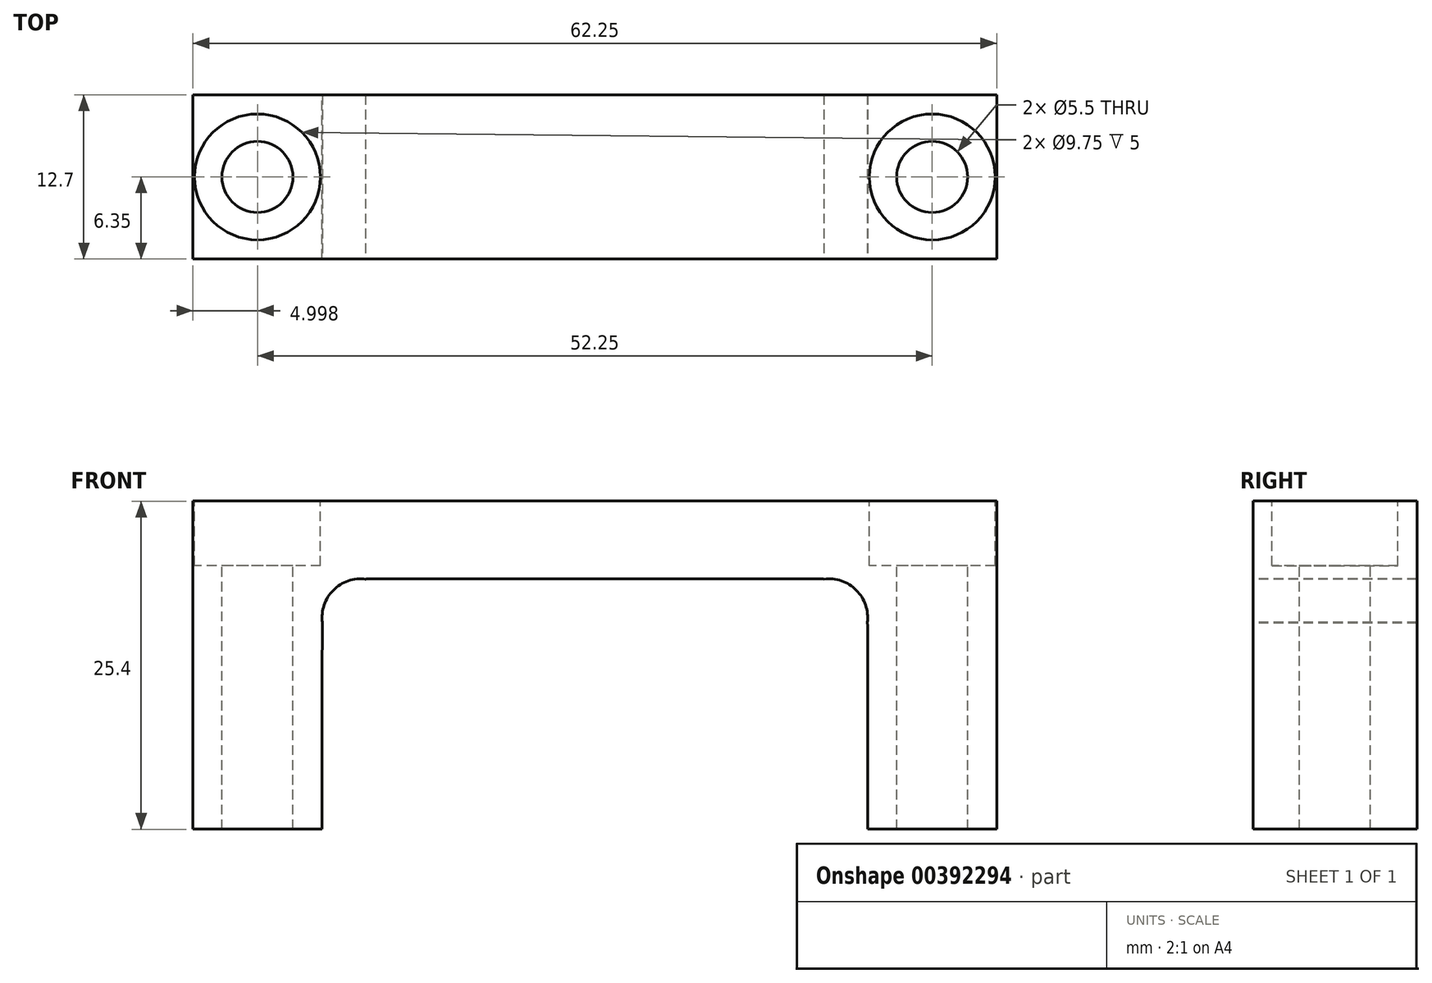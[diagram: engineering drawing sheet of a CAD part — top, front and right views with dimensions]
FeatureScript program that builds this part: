
annotation { "Feature Type Name" : "Feature", "Feature Type Description" : "" }
export const myFeature = defineFeature(function(context is Context, id is Id, definition is map)
    precondition{}
    {
        {
            var Q0;
            Q0=qCreatedBy(makeId("Front.planeOp"),FACE);
            var sketch = newSketch(context, id + "F0", { "sketchPlane" : qUnion([Q0])});
            skLineSegment(sketch, "E0", {"start": v(-31.41, -12.39) * mm, "end": v(-21.41, -12.39) * mm});
            skLineSegment(sketch, "E1", {"start": v(-21.41, -12.39) * mm, "end": v(-21.41, -0.6) * mm});
            skLineSegment(sketch, "E2", {"start": v(-21.41, -0.6) * mm, "end": v(-13.81, 7) * mm});
            skLineSegment(sketch, "E3", {"start": v(-13.81, 7) * mm, "end": v(13.24, 7) * mm});
            skLineSegment(sketch, "E4", {"start": v(13.24, 7) * mm, "end": v(20.84, -0.6) * mm});
            skLineSegment(sketch, "E5", {"start": v(20.84, -0.6) * mm, "end": v(20.84, -12.39) * mm});
            skLineSegment(sketch, "E6", {"start": v(20.84, -12.39) * mm, "end": v(30.84, -12.39) * mm});
            skLineSegment(sketch, "E7", {"start": v(-26.41, 13.01) * mm, "end": v(25.84, 13.01) * mm});
            skLineSegment(sketch, "E8", {"start": v(-31.41, 5.41) * mm, "end": v(-31.41, -12.39) * mm});
            skLineSegment(sketch, "E9", {"start": v(30.84, 5.41) * mm, "end": v(30.84, -12.39) * mm});
            skLineSegment(sketch, "E10", {"start": v(-26.41, 13.01) * mm, "end": v(-31.41, 13.01) * mm});
            skLineSegment(sketch, "E11", {"start": v(-31.41, 13.01) * mm, "end": v(-31.41, 2.42) * mm});
            skLineSegment(sketch, "E12", {"start": v(25.84, 13.01) * mm, "end": v(30.84, 13.01) * mm});
            skLineSegment(sketch, "E13", {"start": v(30.84, 13.01) * mm, "end": v(30.84, 5.41) * mm});
            skSolve(sketch);
        }
        {
            var Q0;
            Q0 = qSketchRegion(id + "F0", true);
            extrude(context, id + "F1", {"entities" : qUnion([Q0]), "endBound" : BoundingType.SYMMETRIC, "depth" : 12.7 * mm});
        }
        {
            var Q0;
            Q0=makeQuery(id+"F1.opExtrude","SWEPT_FACE",FACE,{"disambiguationData":[OSD([sQuery(id+"F0.wireOp",EDGE,"E7"),sQuery(id+"F0.wireOp",EDGE,"E10"),sQuery(id+"F0.wireOp",EDGE,"E12")])]});
            var sketch = newSketch(context, id + "F2", { "sketchPlane" : qUnion([Q0])});
            skPoint(sketch, "E14", {"position": v(-26.41, 0) * mm});
            skPoint(sketch, "E15", {"position": v(25.84, 0) * mm});
            skSolve(sketch);
        }
        {
            var Q0;
            Q0=sQuery(id+"F2.wireOp",VERTEX,"E15");
            var Q1;
            Q1=sQuery(id+"F2.wireOp",VERTEX,"E14");
            var Q2;
            Q2=makeQuery(id+"F1.opExtrude","SWEPT_BODY",BODY,{"disambiguationData":[OSD([sQuery(id+"F0.wireOp",EDGE,"E0"),sQuery(id+"F0.wireOp",EDGE,"E1"),sQuery(id+"F0.wireOp",EDGE,"E2"),sQuery(id+"F0.wireOp",EDGE,"E3"),sQuery(id+"F0.wireOp",EDGE,"E4"),sQuery(id+"F0.wireOp",EDGE,"E5"),sQuery(id+"F0.wireOp",EDGE,"E6"),sQuery(id+"F0.wireOp",EDGE,"E7"),sQuery(id+"F0.wireOp",EDGE,"E8"),sQuery(id+"F0.wireOp",EDGE,"E9"),sQuery(id+"F0.wireOp",EDGE,"E10"),sQuery(id+"F0.wireOp",EDGE,"E11"),sQuery(id+"F0.wireOp",EDGE,"E12"),sQuery(id+"F0.wireOp",EDGE,"E13")])]});
            hole(context, id + "F3", {"style" : HoleStyle.C_BORE, "endStyle" : HoleEndStyle.THROUGH, "standardTappedOrClearance" : lookupTablePath({ "standard" : "ISO", "fit" : "Normal", "size" : "M5", "type" : "Clearance" }), "standardBlindInLast" : lookupTablePath({ "fit" : "Standard", "standard" : "ISO", "size" : "M5", "type" : "Clearance" }), "holeDiameter" : 5.5 * mm, "cBoreDiameter" : 9.75 * mm, "cBoreDepth" : 5 * mm, "isTappedThrough" : true, "tappedDepth" : 12 * mm, "tapClearance" : 3, "startFromSketch" : true, "locations" : qUnion([Q0, Q1]), "scope" : qUnion([Q2])});
        }
        {
            var Q0;
            Q0=makeQuery(id+"F1.opExtrude","CAP_FACE",FACE,{"disambiguationData":[OSD([sQuery(id+"F0.wireOp",EDGE,"E0"),sQuery(id+"F0.wireOp",EDGE,"E1"),sQuery(id+"F0.wireOp",EDGE,"E2"),sQuery(id+"F0.wireOp",EDGE,"E3"),sQuery(id+"F0.wireOp",EDGE,"E4"),sQuery(id+"F0.wireOp",EDGE,"E5"),sQuery(id+"F0.wireOp",EDGE,"E6"),sQuery(id+"F0.wireOp",EDGE,"E7"),sQuery(id+"F0.wireOp",EDGE,"E8"),sQuery(id+"F0.wireOp",EDGE,"E9"),sQuery(id+"F0.wireOp",EDGE,"E10"),sQuery(id+"F0.wireOp",EDGE,"E11"),sQuery(id+"F0.wireOp",EDGE,"E12"),sQuery(id+"F0.wireOp",EDGE,"E13")])],"isStart":false});
            var sketch = newSketch(context, id + "F4", { "sketchPlane" : qUnion([Q0])});
            skCircle(sketch, "E16", {"center": v(-17.61, 3.2) * mm, "radius": 3.8 * mm});
            skLineSegment(sketch, "E17", {"start": v(-13.81, 7) * mm, "end": v(-17.61, 7) * mm});
            skLineSegment(sketch, "E18", {"start": v(-21.41, -0.6) * mm, "end": v(-21.4, 3.57) * mm});
            skCircle(sketch, "E19", {"center": v(17.04, 3.2) * mm, "radius": 3.8 * mm});
            skLineSegment(sketch, "E20", {"start": v(13.24, 7) * mm, "end": v(17.04, 7) * mm});
            skLineSegment(sketch, "E21", {"start": v(20.84, -0.6) * mm, "end": v(20.84, 3.2) * mm});
            skLineSegment(sketch, "E22", {"start": v(20.84, 3.2) * mm, "end": v(20.89, 3.45) * mm});
            skSolve(sketch);
        }
        {
            var Q0;
            {var subQ0=sQuery(id+"F4.wireOp",EDGE,"E17");Q0=makeQuery(id+"F4.imprint","IMPRINT",FACE,{"disambiguationData":[TD([[makeQuery(id+"F4.imprint","IMPRINT",EDGE,{"derivedFrom":subQ0}),1.0]])]});}
            var Q1;
            {var subQ0=sQuery(id+"F4.wireOp",EDGE,"E18");var subQ1=sQuery(id+"F4.wireOp",EDGE,"E16");var subQ2=makeQuery(id+"F4.imprint","INTERSECT",VERTEX,{"disambiguationData":[OD(1.0)],"derivedFrom":[subQ1,subQ0]});Q1=makeQuery(id+"F4.imprint","IMPRINT",FACE,{"disambiguationData":[TD([[makeQuery(id+"F4.imprint","IMPRINT",EDGE,{"disambiguationData":[TD([[subQ2,-1.0]])],"derivedFrom":subQ1}),-1.0]])]});}
            var Q2;
            {var subQ1=sQuery(id+"F4.wireOp",EDGE,"E16");var subQ6=makeQuery(id+"F4.imprint","INTERSECT",VERTEX,{"derivedFrom":[subQ1,sQuery(id+"F4.wireOp",EDGE,"E17")]});Q2=makeQuery(id+"F4.imprint","IMPRINT",FACE,{"disambiguationData":[TD([[makeQuery(id+"F4.imprint","IMPRINT",EDGE,{"disambiguationData":[TD([[subQ6,1.0]])],"derivedFrom":subQ1}),1.0]])]});}
            extrude(context, id + "F5", {"entities" : qUnion([Q0, Q1, Q2]), "operationType" : NewBodyOperationType.REMOVE, "endBound" : BoundingType.THROUGH_ALL, "oppositeDirection" : true, "depth" : 25 * mm});
        }
        {
            var Q0;
            Q0=makeQuery(id+"F1.opExtrude","CAP_FACE",FACE,{"disambiguationData":[OSD([sQuery(id+"F0.wireOp",EDGE,"E0"),sQuery(id+"F0.wireOp",EDGE,"E1"),sQuery(id+"F0.wireOp",EDGE,"E2"),sQuery(id+"F0.wireOp",EDGE,"E3"),sQuery(id+"F0.wireOp",EDGE,"E4"),sQuery(id+"F0.wireOp",EDGE,"E5"),sQuery(id+"F0.wireOp",EDGE,"E6"),sQuery(id+"F0.wireOp",EDGE,"E7"),sQuery(id+"F0.wireOp",EDGE,"E8"),sQuery(id+"F0.wireOp",EDGE,"E9"),sQuery(id+"F0.wireOp",EDGE,"E10"),sQuery(id+"F0.wireOp",EDGE,"E11"),sQuery(id+"F0.wireOp",EDGE,"E12"),sQuery(id+"F0.wireOp",EDGE,"E13")])],"isStart":false});
            var sketch = newSketch(context, id + "F6", { "sketchPlane" : qUnion([Q0])});
            skCircle(sketch, "E23", {"center": v(17.04, 3.2) * mm, "radius": 3.8 * mm});
            skLineSegment(sketch, "E24", {"start": v(13.24, 7) * mm, "end": v(17.04, 7) * mm});
            skLineSegment(sketch, "E25", {"start": v(20.84, -0.6) * mm, "end": v(20.84, 3.2) * mm});
            skSolve(sketch);
        }
        {
            var Q0;
            {var subQ0=sQuery(id+"F6.wireOp",EDGE,"E23");var subQ1=makeQuery(id+"F6.imprint","INTERSECT",VERTEX,{"derivedFrom":[subQ0,sQuery(id+"F6.wireOp",EDGE,"E24")]});Q0=makeQuery(id+"F6.imprint","IMPRINT",FACE,{"disambiguationData":[TD([[makeQuery(id+"F6.imprint","IMPRINT",EDGE,{"disambiguationData":[TD([[subQ1,1.0]])],"derivedFrom":subQ0}),1.0]])]});}
            var Q1;
            {var subQ0=sQuery(id+"F6.wireOp",EDGE,"E24");Q1=makeQuery(id+"F6.imprint","IMPRINT",FACE,{"disambiguationData":[TD([[makeQuery(id+"F6.imprint","IMPRINT",EDGE,{"derivedFrom":subQ0}),-1.0]])]});}
            var Q2;
            {var subQ0=sQuery(id+"F6.wireOp",EDGE,"E25");Q2=makeQuery(id+"F6.imprint","IMPRINT",FACE,{"disambiguationData":[TD([[makeQuery(id+"F6.imprint","IMPRINT",EDGE,{"derivedFrom":subQ0}),1.0]])]});}
            extrude(context, id + "F7", {"entities" : qUnion([Q0, Q1, Q2]), "operationType" : NewBodyOperationType.REMOVE, "endBound" : BoundingType.THROUGH_ALL, "oppositeDirection" : true, "depth" : 25 * mm});
        }
        {
            var Q0;
            Q0=makeQuery(id+"F1.opExtrude","CAP_FACE",FACE,{"disambiguationData":[OSD([sQuery(id+"F0.wireOp",EDGE,"E0"),sQuery(id+"F0.wireOp",EDGE,"E1"),sQuery(id+"F0.wireOp",EDGE,"E2"),sQuery(id+"F0.wireOp",EDGE,"E3"),sQuery(id+"F0.wireOp",EDGE,"E4"),sQuery(id+"F0.wireOp",EDGE,"E5"),sQuery(id+"F0.wireOp",EDGE,"E6"),sQuery(id+"F0.wireOp",EDGE,"E7"),sQuery(id+"F0.wireOp",EDGE,"E8"),sQuery(id+"F0.wireOp",EDGE,"E9"),sQuery(id+"F0.wireOp",EDGE,"E10"),sQuery(id+"F0.wireOp",EDGE,"E11"),sQuery(id+"F0.wireOp",EDGE,"E12"),sQuery(id+"F0.wireOp",EDGE,"E13")])],"isStart":false});
            var sketch = newSketch(context, id + "F8", { "sketchPlane" : qUnion([Q0])});
            skCircle(sketch, "E26", {"center": v(-18.41, 4) * mm, "radius": 3 * mm});
            skCircle(sketch, "E27", {"center": v(17.84, 4) * mm, "radius": 3 * mm});
            skSolve(sketch);
        }
        {
            var Q0;
            {var subQ0=sQuery(id+"F8.wireOp",EDGE,"E26");var subQ1=makeQuery(id+"F5.boolean.opBoolean","COPY",EDGE,{"derivedFrom":makeQuery(id+"F5.opExtrude","CAP_EDGE",EDGE,{"disambiguationData":[OSD([sQuery(id+"F4.wireOp",EDGE,"E16")])],"isStart":true})});var subQ2=makeQuery(id+"F8.imprint","INTERSECT",VERTEX,{"disambiguationData":[OD(0.0)],"derivedFrom":[subQ1,subQ0]});Q0=makeQuery(id+"F8.imprint","IMPRINT",FACE,{"disambiguationData":[TD([[makeQuery(id+"F8.imprint","IMPRINT",EDGE,{"disambiguationData":[TD([[subQ2,-1.0]])],"derivedFrom":subQ0}),1.0]])]});}
            var Q1;
            {var subQ0=sQuery(id+"F8.wireOp",EDGE,"E27");var subQ1=makeQuery(id+"F7.boolean.opBoolean","COPY",EDGE,{"derivedFrom":makeQuery(id+"F7.opExtrude","CAP_EDGE",EDGE,{"disambiguationData":[OSD([sQuery(id+"F6.wireOp",EDGE,"E23")])],"isStart":true})});var subQ2=makeQuery(id+"F8.imprint","INTERSECT",VERTEX,{"disambiguationData":[OD(0.0)],"derivedFrom":[subQ1,subQ0]});Q1=makeQuery(id+"F8.imprint","IMPRINT",FACE,{"disambiguationData":[TD([[makeQuery(id+"F8.imprint","IMPRINT",EDGE,{"disambiguationData":[TD([[subQ2,1.0]])],"derivedFrom":subQ0}),1.0]])]});}
            extrude(context, id + "F9", {"entities" : qUnion([Q0, Q1]), "operationType" : NewBodyOperationType.ADD, "endBound" : BoundingType.THROUGH_ALL, "depth" : 25 * mm});
        }
        {
            var Q0;
            Q0=makeQuery(id+"F9.opExtrude","CAP_FACE",FACE,{"disambiguationData":[OSD([sQuery(id+"F4.wireOp",EDGE,"E16"),sQuery(id+"F8.wireOp",EDGE,"E26")])],"isStart":false});
            var Q1;
            Q1=makeQuery(id+"F9.opExtrude","CAP_FACE",FACE,{"disambiguationData":[OSD([sQuery(id+"F6.wireOp",EDGE,"E23"),sQuery(id+"F8.wireOp",EDGE,"E27")])],"isStart":false});
            extrude(context, id + "F10", {"entities" : qUnion([Q0, Q1]), "operationType" : NewBodyOperationType.REMOVE, "endBound" : BoundingType.THROUGH_ALL, "oppositeDirection" : true, "depth" : 25 * mm});
        }
    });
